# Revit family: MODT060060045CVL
name_source: partatom
category: Specialty Equipment
units: mm (PartAtom-declared; Revit-internal decimal feet)

## family parameters
Always vertical = Yes
Cut with Voids When Loaded = No
OmniClass Number = 23.60.30.17
OmniClass Title = Manholes
Part Type = Normal
Room Calculation Point = No
Round Connector Dimension = Use Diameter
Shared = No
Work Plane-Based = No

## types (1)
- Standard
    Connector_17_Diameter = 110 mm  [stored 0.360892 ft]
    Connector_18_Diameter = 110 mm  [stored 0.360892 ft]
    Connector_19_Diameter = 110 mm  [stored 0.360892 ft]
    Connector_20_Diameter = 110 mm  [stored 0.360892 ft]
    Connector_21_Diameter = 110 mm  [stored 0.360892 ft]
    Connector_22_Diameter = 110 mm  [stored 0.360892 ft]
    Connector_23_Diameter = 110 mm  [stored 0.360892 ft]
    Connector_24_Diameter = 110 mm  [stored 0.360892 ft]
    Connector_25_Diameter = 110 mm  [stored 0.360892 ft]
    Connector_26_Diameter = 110 mm  [stored 0.360892 ft]
    Connector_27_Diameter = 110 mm  [stored 0.360892 ft]
    Connector_28_Diameter = 110 mm  [stored 0.360892 ft]
    Connector_29_Diameter = 110 mm  [stored 0.360892 ft]
    Connector_30_Diameter = 110 mm  [stored 0.360892 ft]
    Connector_31_Diameter = 110 mm  [stored 0.360892 ft]
    Connector_32_Diameter = 110 mm  [stored 0.360892 ft]
    Description = Trekput 600x600x450 C250 Vlak
    Manufacturer = PowerCast BV
    Model = MODT060060045CVL
    URL = https://www.trekput.nl

note: [stored X ft] marks values corroborated as IEEE doubles in the binary element streams (Revit-internal decimal feet)

## geometry (parser evidence)
native form markers: Sweep x1
no freeform markers — native parametric forms only
